# Revit family: 00-7388-05-05
name_source: partatom
category: Luminarias
revit_build: Autodesk Revit 2017 (Build: 20160225_1515(x64)
units: mm (PartAtom-declared; Revit-internal decimal feet)

## family parameters
Anfitrión = Cara
Compartido = Sí
Corte con vacíos al cargar = No
Cota de conector redondo = Diámetro de uso
Número OmniClass = 23.80.70.00
Origen de luz = No
Punto de cálculo de habitación = No
Tipo de pieza = Normal
Título OmniClass = Lighting

## types (1)
- 00-7388-05-05
    Acabado = Negro
    CRI = 0
    Carga aparente = 0 VA
    Catálogo = Decorative
    CodigoGubimclass = 50.60.50.20
    CodigoOmniclass = 21-04 50 40
    CodigoUniclass2015 = EF_70_80
    CodigoUniformat2010 = D5040
    DescripcionGubimclass = Iluminación interior
    DescripcionOmniclass = Lighting
    DescripcionUniclass2015 = Lighting
    DescripcionUniformat2010 = Lighting
    EAN13 = 8435526891238
    Eficiencia energética = NO BULB
    Elevación por defecto = 1000 mm  [stored 3.28084 ft]
    Etiqueta V/f = 100-240V/50-60Hz
    Fabricante = LEDS C4
    Familia = Attic Rectangular Shape
    FechaVersion = Julio 2020
    Ficha = http://files.leds-c4.com
    Fotometría = http://files.leds-c4.com
    IMC = http://files.leds-c4.com
    IP = IP20
    IfcExportAs = IfcLightFixture
IfcLightFixture
    IfcExportType = NOTDEFINED
    Imagen web = http://files.leds-c4.com
    LDT = http://files.leds-c4.com
    Lumenes reales (lm) = 0
    Material = Aluminio
    Peso neto (KG) = 0
    Pluma comercial = http://files.leds-c4.com
    Producto descatalogado = Catalogado ES
    Referencia = 00-7388-05-05
    Tender text (Castellano) = LEDS C4
Attic Rectangular Shape
00-7388-05-05

Colgante de uso interior y exterior para iluminar hacia abajo. 

Diseño de Nahtrang. Ideal composiciones deco-tech. Diseño atemporal. Muy versátil. Múltiples instalaciones. Muy customizable: accesorios, acabados… Sin tornillos a la vista. Òptimo precio-rendimiento. Fácil instalación. Alta durabilidad para uso intensivo. Material estructura: Aluminio. Acabado estructura: Negro. Garantía: 5 Años.

Peso neto del producto (Kg): 0.000
Anchura o diámetro del producto (mm): 150
Altura del producto (mm): 2500

Clase 2. IP: IP20. E27. Longitud máxima de la bombilla que admite la luminaria: 120. Diámetro máximo de la bombilla que admite la luminaria: 100. Nº de portalámparas o Leds: 1. Potencia máxima de la fuente de luz: 23W. Equipo incluido: No. Potencia total: 23. Factor de potencia: 1.00.
    Tender text (English) = LEDS C4
Attic Rectangular Shape
00-7388-05-05

Pendant for indoor and outdoor use. 

For downlighting. Design by Nahtrang. Ideal deco-tech compositions. Timeless design. Highly versatile, multiple installations. Highly customisable: accessories, finishes… No visible screws. Optimum price-performance. Easy instalation. High durability for intensive use. Structure material: Aluminium. Structure finish: Black. Warranty: 5 Years.

Product net weight (Kg): 0.000
Product width or diameter (mm): 150
Product height (mm): 2500

Class 2. IP: IP20. E27. Maximum length of luminaire bulb: 120. Maximum diameter of luminaire bulb: 100. No. of lampholders or LEDs: 1. Maximum power of light source: 23W. Gear included: No. Total power: 23. Power factor: 1.00.
    Tipo = Colgante
    Vatios (W) = 23
    Versión = v1

note: [stored X ft] marks values corroborated as IEEE doubles in the binary element streams (Revit-internal decimal feet)
